# Revit family: Maxlogic İtfaiyeci telefon kontrol ünitesi
name_source: partatom
category: Fire Alarm Devices
units: mm (PartAtom-declared; Revit-internal decimal feet)

## family parameters
Cut with Voids When Loaded = No
Host = Face
Maintain Annotation Orientation = Yes
OmniClass Number = 23.85.30.21
OmniClass Title = Environmental Detection/Registration
Part Type = Normal
Room Calculation Point = No
Round Connector Dimension = Use Diameter
Shared = No

## types (3) — shared parameters
Color = Beyaz
External supply = 230 V AC
Fax Number = (+)90 216 466 45 10
Installation Manual = https://mavilielektronik.com
Main Material = Metal Grey
Manufacturer = Mavili Elektronik Ticaret A.Ş.
Model = Maxlogic
Mounting surface = Duvara montaj
Nominal Depth = 140 mm
Nominal Height = 370 mm
Nominal Width = 500 mm
Operating temperature = (-10°C) - (+50°C)
Secondary Material = White Plastic ABS
URL = https://www.mavili.com.tr
Warranty Duration Labor = 2
Warranty Duration Parts = 2
Warranty Duration Unit = Year
zero-valued in all types: Cost, Default Elevation

## per-type parameters (varying)
| type | Description | Product Code |
| Maxlogic İtfaiyeci Telefon Kontrol Ünitesi, 8 telefon modülü kapasiteli | İtfaiyeci Telefon Kontrol Ünitesi, 8 telefon modülü kapasiteli | ML-50108 |
| Maxlogic İtfaiyeci Telefon Kontrol Ünitesi, 16 telefon modülü kapasiteli | İtfaiyeci Telefon Kontrol Ünitesi, 16 telefon modülü kapasiteli | ML-50116 |
| Maxlogic İtfaiyeci Telefon Kontrol Ünitesi, 32 telefon modülü kapasiteli | İtfaiyeci Telefon Kontrol Ünitesi, 32 telefon modülü kapasiteli | ML-50132 |

## geometry (parser evidence)
native form markers: Sweep x1
no freeform markers — native parametric forms only
